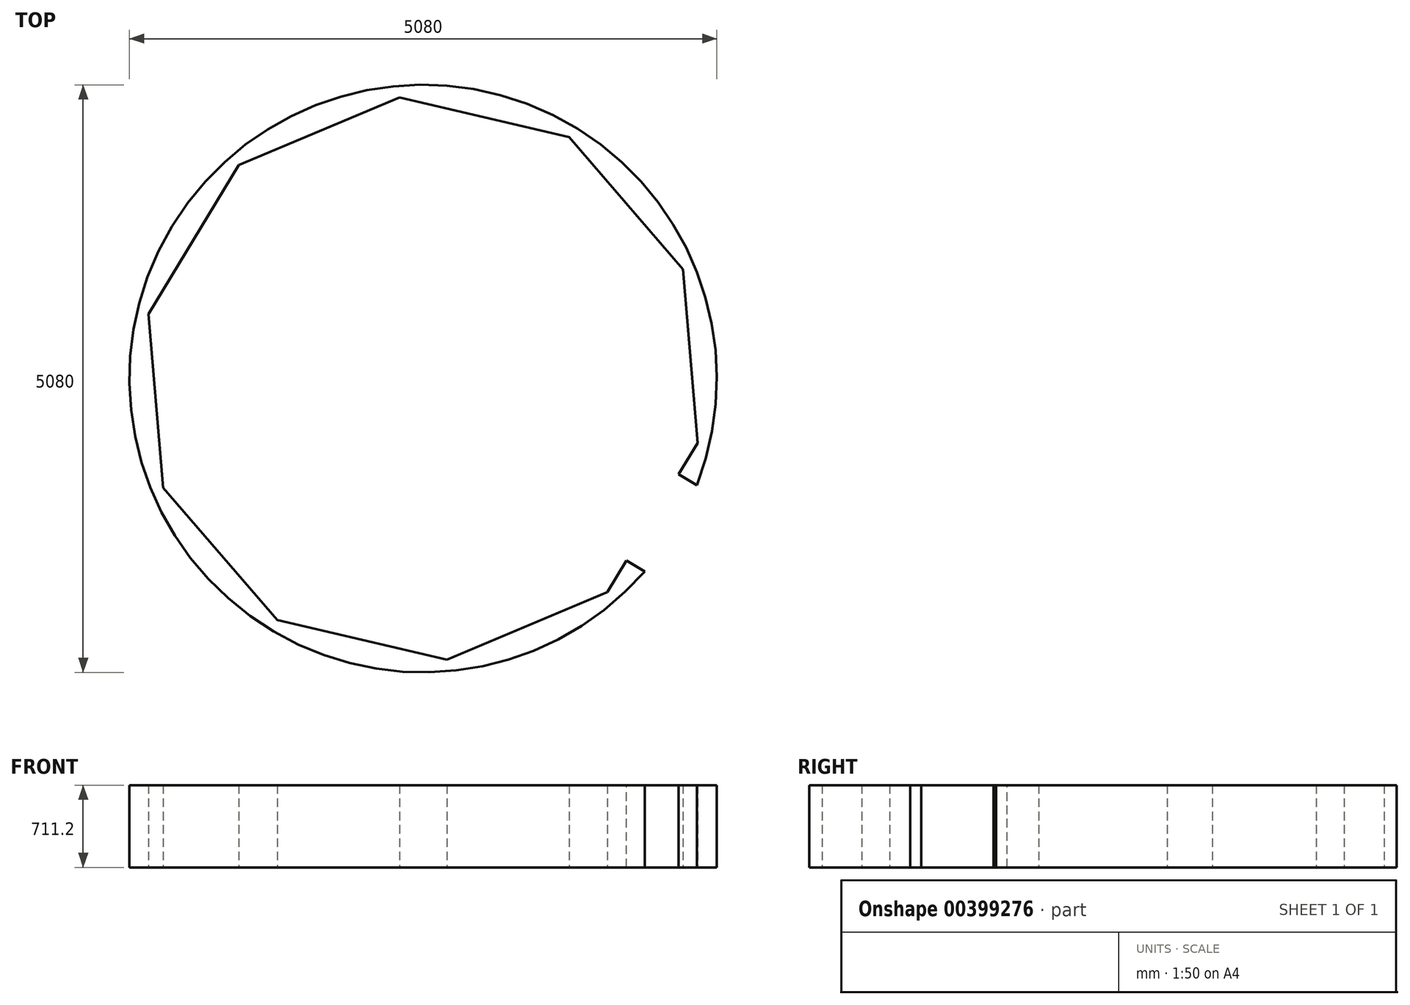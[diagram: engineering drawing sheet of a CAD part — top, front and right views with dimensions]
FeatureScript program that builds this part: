
annotation { "Feature Type Name" : "Feature", "Feature Type Description" : "" }
export const myFeature = defineFeature(function(context is Context, id is Id, definition is map)
    precondition{}
    {
        {
            var Q0;
            Q0=qCreatedBy(makeId("Top.planeOp"),FACE);
            var sketch = newSketch(context, id + "F0", { "sketchPlane" : qUnion([Q0])});
            skCircle(sketch, "E0.cCircle", {"center": v(0, 0) * mm, "radius": 2438.4 * mm, "construction": true});
            skLineSegment(sketch, "E0.0", {"start": v(204.96, -2429.77) * mm, "end": v(-1262.36, -2086.2) * mm});
            skLineSegment(sketch, "E0.1", {"start": v(-1262.36, -2086.2) * mm, "end": v(-2247.51, -945.77) * mm});
            skLineSegment(sketch, "E0.2", {"start": v(-2247.51, -945.77) * mm, "end": v(-2374.19, 555.9) * mm});
            skLineSegment(sketch, "E0.3", {"start": v(-2374.19, 555.9) * mm, "end": v(-1594, 1845.25) * mm});
            skLineSegment(sketch, "E0.4", {"start": v(-1594, 1845.25) * mm, "end": v(-204.96, 2429.77) * mm});
            skLineSegment(sketch, "E0.5", {"start": v(-204.96, 2429.77) * mm, "end": v(1262.36, 2086.2) * mm});
            skLineSegment(sketch, "E0.6", {"start": v(1262.36, 2086.2) * mm, "end": v(2247.51, 945.77) * mm});
            skLineSegment(sketch, "E0.7", {"start": v(2247.51, 945.77) * mm, "end": v(2374.19, -555.9) * mm});
            skLineSegment(sketch, "E0.8", {"start": v(2374.19, -555.9) * mm, "end": v(1594, -1845.25) * mm});
            skLineSegment(sketch, "E0.9", {"start": v(1594, -1845.25) * mm, "end": v(204.96, -2429.77) * mm});
            skLineSegment(sketch, "E1", {"start": v(0, 0) * mm, "end": v(-1262.36, -2086.2) * mm, "construction": true});
            skLineSegment(sketch, "E2", {"start": v(-1262.36, -2086.2) * mm, "end": v(-1692.79, -2797.52) * mm, "construction": true});
            skLineSegment(sketch, "E3", {"start": v(0, 0) * mm, "end": v(1629.92, 2693.64) * mm, "construction": true});
            skLineSegment(sketch, "E4", {"start": v(-204.96, 2429.77) * mm, "end": v(204.96, -2429.77) * mm, "construction": true});
            skLineSegment(sketch, "E5", {"start": v(-1594, 1845.25) * mm, "end": v(-204.96, 2429.77) * mm, "construction": true});
            skLineSegment(sketch, "E6", {"start": v(-204.96, 2429.77) * mm, "end": v(-249.8, 2961.38) * mm, "construction": true});
            skLineSegment(sketch, "E7", {"start": v(-2247.51, -945.77) * mm, "end": v(2247.51, 945.77) * mm, "construction": true});
            skLineSegment(sketch, "E8", {"start": v(2247.51, 945.77) * mm, "end": v(3026.37, 1273.52) * mm, "construction": true});
            skLineSegment(sketch, "E9", {"start": v(-2247.51, -945.77) * mm, "end": v(-2964.67, -1247.56) * mm, "construction": true});
            skLineSegment(sketch, "E10", {"start": v(204.96, -2429.77) * mm, "end": v(257.65, -3054.33) * mm, "construction": true});
            skLineSegment(sketch, "E11", {"start": v(0, 0) * mm, "end": v(1594, -1845.25) * mm, "construction": true});
            skLineSegment(sketch, "E12", {"start": v(-1594, 1845.25) * mm, "end": v(0, 0) * mm, "construction": true});
            skLineSegment(sketch, "E13", {"start": v(1594, -1845.25) * mm, "end": v(1870.17, -2164.94) * mm, "construction": true});
            skLineSegment(sketch, "E14", {"start": v(1870.17, -2164.94) * mm, "end": v(-1594, 1845.25) * mm, "construction": true});
            skLineSegment(sketch, "E15", {"start": v(-1594, 1845.25) * mm, "end": v(-2117.15, 2450.85) * mm, "construction": true});
            skLineSegment(sketch, "E16", {"start": v(-2117.15, 2450.85) * mm, "end": v(0, 0) * mm, "construction": true});
            skLineSegment(sketch, "E17", {"start": v(-2367.75, 541.62) * mm, "end": v(0, 0) * mm, "construction": true});
            skLineSegment(sketch, "E18", {"start": v(-2374.19, 555.9) * mm, "end": v(-2974.53, 693.24) * mm, "construction": true});
            skLineSegment(sketch, "E19", {"start": v(-2974.53, 693.24) * mm, "end": v(0, 0) * mm, "construction": true});
            skLineSegment(sketch, "E20", {"start": v(0, 0) * mm, "end": v(2374.19, -555.9) * mm, "construction": true});
            skLineSegment(sketch, "E21", {"start": v(2374.19, -555.9) * mm, "end": v(2821.15, -555.9) * mm, "construction": true});
            skLineSegment(sketch, "E22", {"start": v(2374.19, -555.9) * mm, "end": v(3090.95, -723.73) * mm, "construction": true});
            skCircle(sketch, "E23", {"center": v(0, 0) * mm, "radius": 2540 * mm});
            skSolve(sketch);
        }
        {
            var Q0;
            Q0 = qSketchRegion(id + "F0", true);
            extrude(context, id + "F1", {"entities" : qUnion([Q0]), "depth" : 711.2 * mm});
        }
        {
            var Q0;
            Q0=makeQuery(id+"F1.opExtrude","SWEPT_FACE",FACE,{"disambiguationData":[OSD([sQuery(id+"F0.wireOp",EDGE,"E0.8")])]});
            var sketch = newSketch(context, id + "F2", { "sketchPlane" : qUnion([Q0])});
            skLineSegment(sketch, "E24.bottom", {"start": v(-435.17, 711.2) * mm, "end": v(435.17, 711.2) * mm});
            skLineSegment(sketch, "E24.top", {"start": v(-435.17, 0) * mm, "end": v(435.17, 0) * mm});
            skLineSegment(sketch, "E24.left", {"start": v(-435.17, 0) * mm, "end": v(-435.17, 711.2) * mm});
            skLineSegment(sketch, "E24.right", {"start": v(435.17, 0) * mm, "end": v(435.17, 711.2) * mm});
            skPoint(sketch, "E24.middle", {"position": v(0, 355.6) * mm});
            skPoint(sketch, "E24.middle.positionSnap0", {"position": v(-753.5, 355.6) * mm});
            skPoint(sketch, "E24.centerSnap0", {"position": v(-753.5, 355.6) * mm});
            skSolve(sketch);
        }
        {
            var Q0;
            Q0 = qSketchRegion(id + "F2", true);
            extrude(context, id + "F3", {"entities" : qUnion([Q0]), "operationType" : NewBodyOperationType.REMOVE, "oppositeDirection" : true, "depth" : 922.9 * mm});
        }
    });
